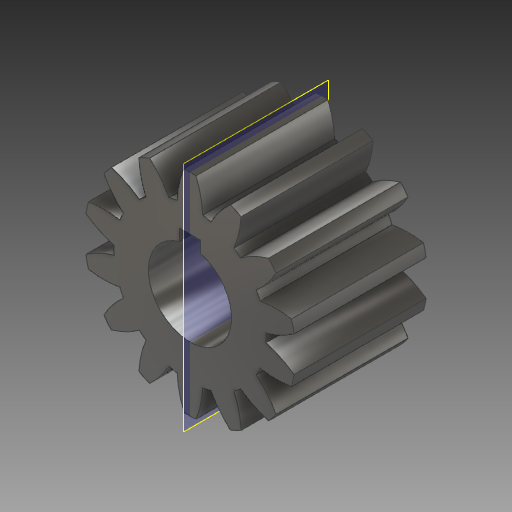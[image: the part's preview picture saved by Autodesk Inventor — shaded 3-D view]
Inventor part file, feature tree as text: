
AUTODESK INVENTOR PART (.ipt)
format: ipt  version: 2017.1 (Build 211199000, 199)  size: 248,320 bytes
history: native  units: in
note: dims shown in document units (in); Inventor stores cm internally (conversion verified against a paired STEP export)
features: plane x1, imported_body x1
ambient origin geometry x8: Origin, YZ Plane, XZ Plane, XY Plane, X Axis, Y Axis, Z Axis, Center Point
bodies: Solid1 (feature_tree)
feature tree (2):
  plane  "Work Plane3"
  imported_body  "Imported1"
